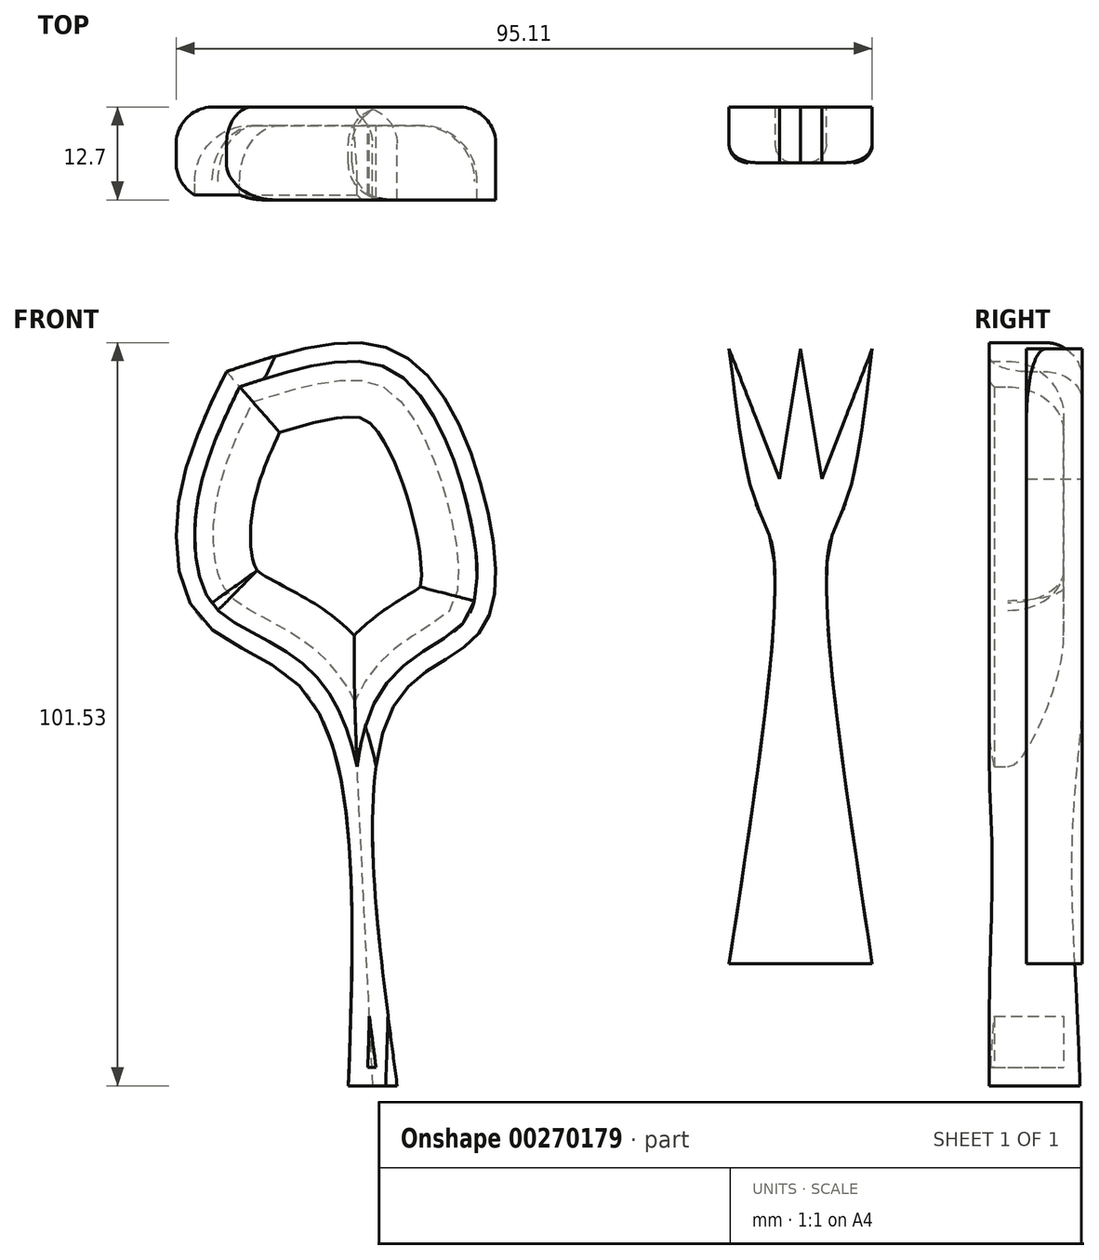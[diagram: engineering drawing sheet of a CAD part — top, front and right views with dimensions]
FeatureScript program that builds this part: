
annotation { "Feature Type Name" : "Feature", "Feature Type Description" : "" }
export const myFeature = defineFeature(function(context is Context, id is Id, definition is map)
    precondition{}
    {
        {
            var Q0;
            Q0=qCreatedBy(makeId("Front.planeOp"),FACE);
            var sketch = newSketch(context, id + "F0", { "sketchPlane" : qUnion([Q0])});
            skFitSpline(sketch, "E0", {"points": [v(-56.45, 47.56) * mm, v(-62.9, 30.23) * mm, v(-59.79, 13.56) * mm, v(-45.34, 3.33) * mm, v(-39.78, -50) * mm], "startDerivative": vector(-37.7, -76.79) * mm, "endDerivative": vector(-6.5, -180.54) * mm});
            skLineSegment(sketch, "E1", {"start": v(-39.78, -50) * mm, "end": v(-33.12, -50) * mm});
            skFitSpline(sketch, "E2", {"points": [v(-33.12, -50) * mm, v(-33.12, 2.67) * mm, v(-21.78, 12) * mm, v(-21.11, 30) * mm, v(-33.12, 50.23) * mm, v(-56.45, 47.56) * mm], "startDerivative": vector(-30.32, 226.28) * mm, "endDerivative": vector(-132.98, -44.05) * mm});
            skSolve(sketch);
        }
        {
            var Q0;
            Q0 = qSketchRegion(id + "F0", true);
            extrude(context, id + "F1", {"entities" : qUnion([Q0]), "depth" : 12.7 * mm});
        }
        {
            var Q0;
            Q0=makeQuery(id+"F1.opExtrude","CAP_FACE",FACE,{"disambiguationData":[OSD([sQuery(id+"F0.wireOp",EDGE,"E0"),sQuery(id+"F0.wireOp",EDGE,"E1"),sQuery(id+"F0.wireOp",EDGE,"E2")])],"isStart":false});
            shell(context, id + "F2", {"entities" : qUnion([Q0]), "thickness" : 2.54 * mm});
        }
        {
            var Q0;
            Q0=makeQuery(id+"F2.opShell","OFFSET_FACE",FACE,{"disambiguationData":[OSD([sQuery(id+"F0.wireOp",EDGE,"E0"),sQuery(id+"F0.wireOp",EDGE,"E1"),sQuery(id+"F0.wireOp",EDGE,"E2")]),OD(0.0)]});
            fillet(context, id + "F3", {"entities" : qUnion([Q0]), "radius" : 7.62 * mm, "tangentPropagation" : true, "allowEdgeOverflow" : false});
        }
        {
            var Q0;
            Q0=makeQuery(id+"F1.opExtrude","CAP_EDGE",EDGE,{"disambiguationData":[OSD([sQuery(id+"F0.wireOp",EDGE,"E0")])],"isStart":false});
            var Q1;
            Q1=makeQuery(id+"F1.opExtrude","CAP_EDGE",EDGE,{"disambiguationData":[OSD([sQuery(id+"F0.wireOp",EDGE,"E2")])],"isStart":true});
            var Q2;
            Q2=makeQuery(id+"F1.opExtrude","CAP_EDGE",EDGE,{"disambiguationData":[OSD([sQuery(id+"F0.wireOp",EDGE,"E0")])],"isStart":true});
            fillet(context, id + "F4", {"entities" : qUnion([Q0, Q1, Q2]), "radius" : 5.08 * mm, "tangentPropagation" : true, "allowEdgeOverflow" : false});
        }
        {
            var Q0;
            Q0=qCreatedBy(makeId("Front.planeOp"),FACE);
            var sketch = newSketch(context, id + "F5", { "sketchPlane" : qUnion([Q0])});
            skFitSpline(sketch, "E3", {"points": [v(12.22, 50.67) * mm, v(15.78, 29.78) * mm, v(18.22, 23.11) * mm, v(12.22, -33.34) * mm], "startDerivative": vector(9.66, -80.09) * mm, "endDerivative": vector(-21.54, -140.95) * mm});
            skLineSegment(sketch, "E4", {"start": v(12.22, -33.34) * mm, "end": v(31.78, -33.34) * mm});
            skLineSegment(sketch, "E5", {"start": v(12.22, 50.67) * mm, "end": v(19.11, 32.9) * mm});
            skLineSegment(sketch, "E6", {"start": v(19.11, 32.9) * mm, "end": v(22, 50.67) * mm});
            skLineSegment(sketch, "E7.MirrorCS", {"start": v(24.9, 32.9) * mm, "end": v(22, 50.67) * mm});
            skLineSegment(sketch, "E8.MirrorCS", {"start": v(31.78, 50.67) * mm, "end": v(24.9, 32.9) * mm});
            skFitSpline(sketch, "E9.MirrorCS", {"points": [v(31.78, 50.67) * mm, v(28.23, 29.78) * mm, v(25.78, 23.11) * mm, v(31.78, -33.34) * mm], "startDerivative": vector(-9.66, -80.09) * mm, "endDerivative": vector(21.54, -140.95) * mm});
            skLineSegment(sketch, "E10.MirrorCS", {"start": v(31.78, -33.34) * mm, "end": v(12.22, -33.34) * mm});
            skPoint(sketch, "E11.orphan", {"position": v(-6, -33.34) * mm});
            skPoint(sketch, "E12.orphan", {"position": v(50, -33.34) * mm});
            skSolve(sketch);
        }
        {
            var Q0;
            Q0=makeQuery(id+"F5.imprint","IMPRINT",FACE,{"disambiguationData":[TD([[makeQuery(id+"F5.imprint","IMPRINT",EDGE,{"derivedFrom":sQuery(id+"F5.wireOp",EDGE,"E3")}),1.0]])]});
            extrude(context, id + "F6", {"entities" : qUnion([Q0]), "depth" : 7.62 * mm});
        }
        {
            var Q0;
            Q0=makeQuery(id+"F6.opExtrude","CAP_EDGE",EDGE,{"disambiguationData":[OSD([sQuery(id+"F5.wireOp",EDGE,"E3")])],"isStart":false});
            var Q1;
            Q1=makeQuery(id+"F6.opExtrude","CAP_EDGE",EDGE,{"disambiguationData":[OSD([sQuery(id+"F5.wireOp",EDGE,"E10.MirrorCS")])],"isStart":false});
            var Q2;
            Q2=makeQuery(id+"F6.opExtrude","CAP_EDGE",EDGE,{"disambiguationData":[OSD([sQuery(id+"F5.wireOp",EDGE,"E9.MirrorCS")])],"isStart":false});
            fillet(context, id + "F7", {"entities" : qUnion([Q0, Q1, Q2]), "radius" : 2.54 * mm, "tangentPropagation" : true, "allowEdgeOverflow" : false});
        }
    });
